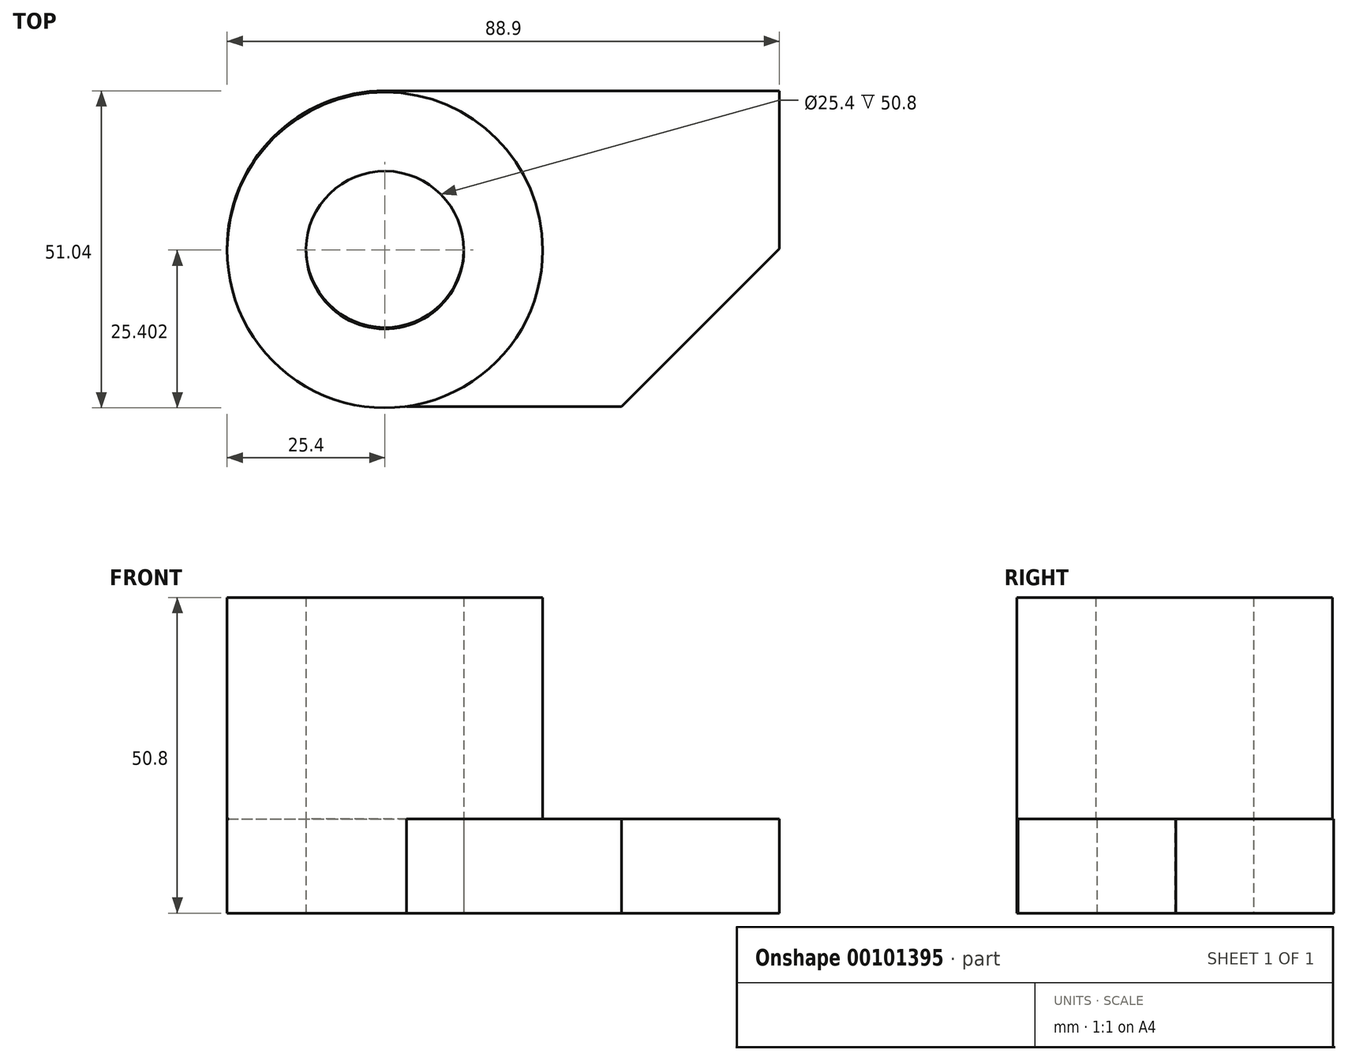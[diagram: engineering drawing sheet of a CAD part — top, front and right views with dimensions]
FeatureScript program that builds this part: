
annotation { "Feature Type Name" : "Feature", "Feature Type Description" : "" }
export const myFeature = defineFeature(function(context is Context, id is Id, definition is map)
    precondition{}
    {
        {
            var Q0;
            Q0=qCreatedBy(makeId("Front.planeOp"),FACE);
            var sketch = newSketch(context, id + "F0", { "sketchPlane" : qUnion([Q0])});
            skLineSegment(sketch, "E0", {"start": v(0, 0) * mm, "end": v(88.9, 0) * mm});
            skLineSegment(sketch, "E1", {"start": v(88.9, 0) * mm, "end": v(88.9, 15.17) * mm});
            skLineSegment(sketch, "E2", {"start": v(38.1, 15.17) * mm, "end": v(88.9, 15.17) * mm});
            skPoint(sketch, "E3", {"position": v(63.5, 0) * mm});
            skPoint(sketch, "E4", {"position": v(38.1, 0) * mm});
            skLineSegment(sketch, "E5", {"start": v(38.1, 15.17) * mm, "end": v(38.1, 15.17) * mm});
            skLineSegment(sketch, "E6", {"start": v(38.1, 15.17) * mm, "end": v(0, 15.17) * mm});
            skLineSegment(sketch, "E7", {"start": v(0, 0) * mm, "end": v(0, 15.17) * mm});
            skSolve(sketch);
        }
        {
            var Q0;
            Q0=qCreatedBy(makeId("Top.planeOp"),FACE);
            var sketch = newSketch(context, id + "F1", { "sketchPlane" : qUnion([Q0])});
            skCircle(sketch, "E8", {"center": v(25.4, 25.4) * mm, "radius": 25.4 * mm});
            skLineSegment(sketch, "E9", {"start": v(25.4, 0) * mm, "end": v(63.5, 0) * mm});
            skLineSegment(sketch, "E10", {"start": v(63.5, 0) * mm, "end": v(88.9, 25.4) * mm});
            skLineSegment(sketch, "E11", {"start": v(88.9, 25.4) * mm, "end": v(88.9, 50.8) * mm});
            skLineSegment(sketch, "E12", {"start": v(88.9, 50.8) * mm, "end": v(25.4, 50.8) * mm});
            skLineSegment(sketch, "E13", {"start": v(0, 25.4) * mm, "end": v(0, 25.4) * mm});
            skCircle(sketch, "E14", {"center": v(25.4, 25.4) * mm, "radius": 12.7 * mm});
            skPoint(sketch, "E15.visualSharp", {"position": v(0, 50.8) * mm});
            skArc(sketch, "E15.filletArc", {"start": v(25.4, 50.8) * mm, "mid": v(7.44, 43.36) * mm, "end": v(0, 25.4) * mm});
            skPoint(sketch, "E16.visualSharp", {"position": v(0, 0) * mm});
            skArc(sketch, "E16.filletArc", {"start": v(0, 25.4) * mm, "mid": v(7.44, 7.44) * mm, "end": v(25.4, 0) * mm});
            skPoint(sketch, "E17", {"position": v(50.8, 25.75) * mm});
            skLineSegment(sketch, "E18", {"start": v(50.8, 25.75) * mm, "end": v(50.8, 25.75) * mm});
            skLineSegment(sketch, "E19", {"start": v(25.4, 50.8) * mm, "end": v(25.4, 50.8) * mm});
            skLineSegment(sketch, "E20", {"start": v(25.4, 0) * mm, "end": v(25.4, 0) * mm});
            skPoint(sketch, "E21.visualSharp", {"position": v(51.15, 0) * mm});
            skArc(sketch, "E21.filletArc", {"start": v(25.4, 0) * mm, "mid": v(43.48, 7.56) * mm, "end": v(50.8, 25.75) * mm});
            skPoint(sketch, "E22.visualSharp", {"position": v(50.46, 50.8) * mm});
            skArc(sketch, "E22.filletArc", {"start": v(50.8, 25.75) * mm, "mid": v(43.24, 43.48) * mm, "end": v(25.4, 50.8) * mm});
            skLineSegment(sketch, "E23", {"start": v(51.15, 0) * mm, "end": v(25.4, 0) * mm});
            skLineSegment(sketch, "E24", {"start": v(25.4, 50.8) * mm, "end": v(50.46, 50.8) * mm});
            skSolve(sketch);
        }
        {
            var Q0;
            Q0 = qSketchRegion(id + "F0", true);
            extrude(context, id + "F2", {"entities" : qUnion([Q0]), "oppositeDirection" : true, "depth" : 50.8 * mm});
        }
        {
            var Q0;
            Q0 = qSketchRegion(id + "F1", true);
            extrude(context, id + "F3", {"entities" : qUnion([Q0]), "operationType" : NewBodyOperationType.INTERSECT, "depth" : 50.8 * mm});
        }
        {
            var Q0;
            Q0=qCreatedBy(makeId("Top.planeOp"),FACE);
            var sketch = newSketch(context, id + "F4", { "sketchPlane" : qUnion([Q0])});
            skCircle(sketch, "E25", {"center": v(25.4, 25.16) * mm, "radius": 25.4 * mm});
            skCircle(sketch, "E26", {"center": v(25.4, 25.16) * mm, "radius": 12.7 * mm});
            skSolve(sketch);
        }
        {
            var Q0;
            Q0 = qSketchRegion(id + "F4", true);
            extrude(context, id + "F5", {"entities" : qUnion([Q0]), "operationType" : NewBodyOperationType.ADD, "depth" : 50.8 * mm});
        }
    });
